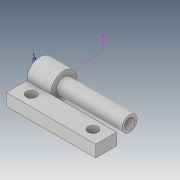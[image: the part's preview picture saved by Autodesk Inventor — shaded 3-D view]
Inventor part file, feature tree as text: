
AUTODESK INVENTOR PART (.ipt)
format: ipt  version: 2019 (Build 230136000, 136)  size: 269,824 bytes
history: native  units: mm
features: other x13, extrude x8, sketch x7, plane x5, direct_edit x3, projected_geometry x2, move_body x2, fillet x1
ambient origin geometry x8: Origin, YZ Plane, XZ Plane, XY Plane, X Axis, Y Axis, Z Axis, Center Point
bodies: Solid1 (feature_tree)
feature tree (41):
  other  "Annotations"
  extrude  "Extrusion1"  Depth=45.0mm
  sketch  "Sketch4"  dims[d5=5.0mm d6=5.0mm d7=11.0mm]
  extrude  "Extrusion4"  Depth=5.0mm
  fillet  "Fillet1"  Radius=11.0mm
  extrude  "Extrusion5"  Depth=23.0mm
  plane  "Work Plane1"
  extrude  "Extrusion6"  Depth=10.0mm
  plane  "Work Plane8"
  plane  "Work Plane10"
  sketch  "Sketch11"  dims[d24=3.0mm d25=0.0mm d26=12.0mm]
  plane  "Work Plane11"
  plane  "Work Plane12"
  extrude  "Extrusion10"  Depth=12.0mm
  extrude  "Extrusion11"  Depth=3.0mm TaperAngle=0.0deg
  direct_edit  "Direct Edit1"
  extrude  "Extrusion13"  Depth=6.5mm
  direct_edit  "Direct Edit2"
  sketch  "Sketch15"  dims[d33=5.0mm d34=5.0mm d35=17.8mm d36=7.0mm d37=18.0mm d38=7.1mm d39=30.8mm d40=7.100649mm d41=3.0mm d42=0.0mm d52=0.0mm d53=0.0mm d54=0.0mm d55=10.0mm d56=0.0mm d57=10.0mm d58=0.0mm d59=0.0mm d60=0.0mm d61=-1.5mm d62=0.0mm d63=0.0mm d64=-17.25mm d68=1.6mm d69=10.0mm d70=0.0mm d77=-0.3mm d78=2.5mm d79=0.0mm d80=0.5mm d71=35.626875mm d72=6.5mm d75=48.705644mm d76=7.6mm]
  extrude  "Extrusion14"  Depth=6.5mm
  direct_edit  "Direct Edit3"
  sketch  "Sketch1"  dims[d0=6.0mm d1=0.0mm d4=45.0mm]
  sketch  "Sketch5"  dims[d8=11.0mm d9=23.0mm]
  sketch  "Sketch6"  dims[d10=10.0mm d20=13.0mm]
  projected_geometry  "Projected Loop4"
  sketch  "Sketch13"  dims[d27=5.0mm d28=3.0mm d29=0.0mm]
  projected_geometry  "Projected Loop5"
  other  "Composite2"
  move_body  "Move1"
  move_body  "Move2"
  other  "Size1"
  other  "Srf2"
  other  "Size2"
  other  "Radial Dimension 1"
  other  "Diameter Dimension 1"
  parser-record x2  (decoder bookkeeping rows leaked as tree rows — omitted from the tree; the rows remain in map.json)
  other  "Cerniera Assemb.iam"
  other  "Cerniera 1:2"
  other  "Cerniera_definitiva.iam"
  other  "Cerniera_cov:1"
note: 2 file-system paths scrubbed to <path> (originals preserved in map.json)
